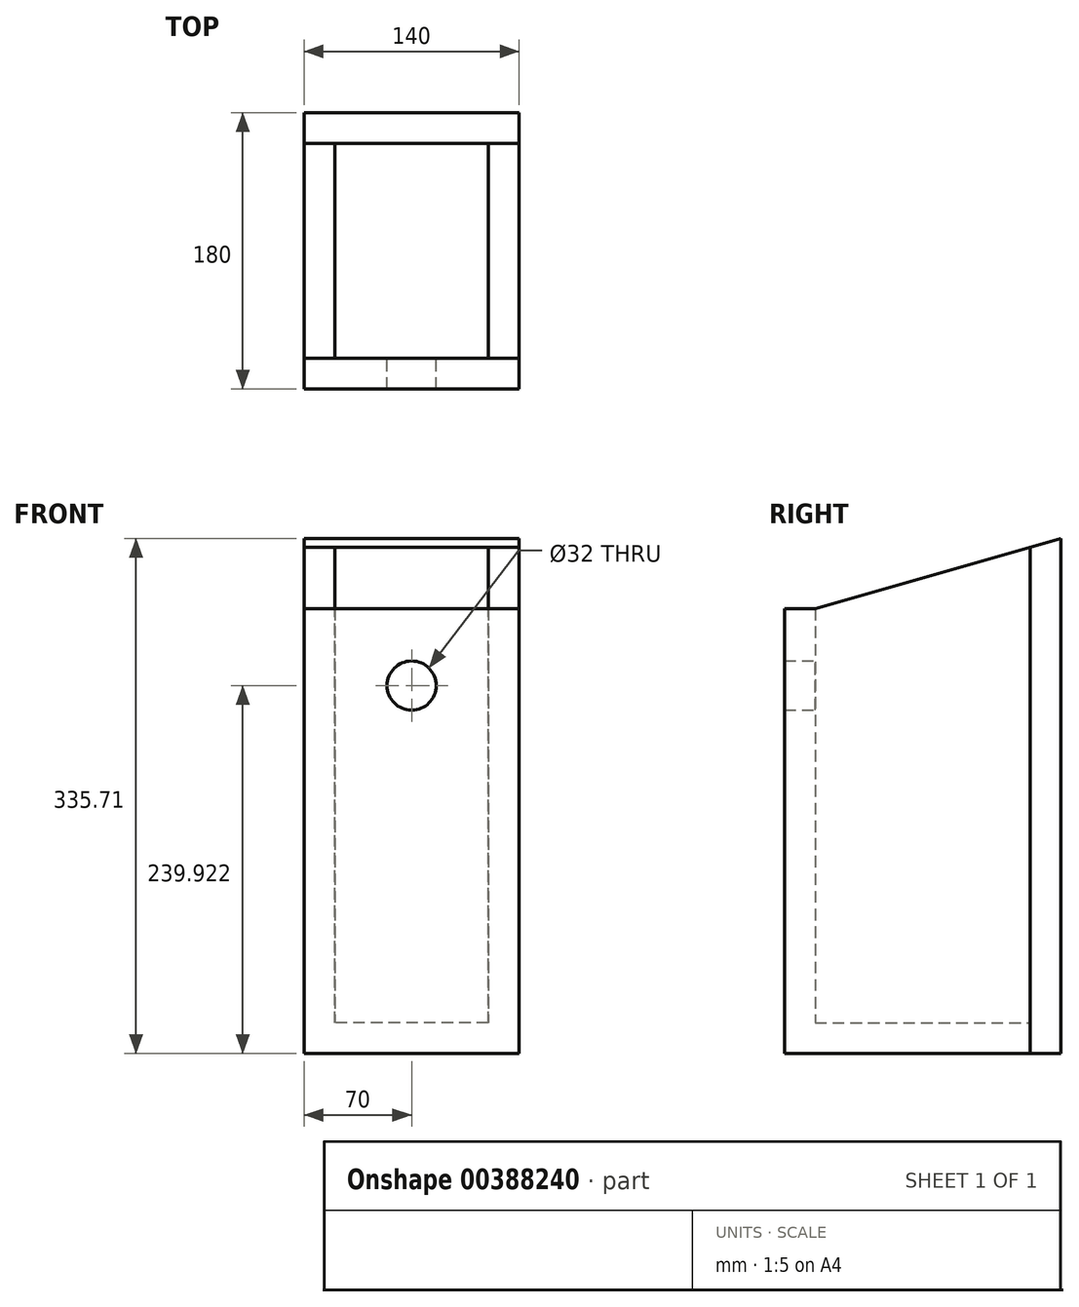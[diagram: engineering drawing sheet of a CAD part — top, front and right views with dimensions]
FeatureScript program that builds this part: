
annotation { "Feature Type Name" : "Feature", "Feature Type Description" : "" }
export const myFeature = defineFeature(function(context is Context, id is Id, definition is map)
    precondition{}
    {
        {
            var Q0;
            Q0=qCreatedBy(makeId("Top.planeOp"),FACE);
            var sketch = newSketch(context, id + "F0", { "sketchPlane" : qUnion([Q0])});
            skLineSegment(sketch, "E0.bottom", {"start": v(50, -70) * mm, "end": v(-50, -70) * mm});
            skLineSegment(sketch, "E0.top", {"start": v(50, 70) * mm, "end": v(-50, 70) * mm});
            skLineSegment(sketch, "E0.left", {"start": v(50, -70) * mm, "end": v(50, 70) * mm});
            skLineSegment(sketch, "E0.right", {"start": v(-50, -70) * mm, "end": v(-50, 70) * mm});
            skPoint(sketch, "E0.middle", {"position": v(0, 0) * mm});
            skSolve(sketch);
        }
        {
            var Q0;
            Q0 = qSketchRegion(id + "F0", true);
            extrude(context, id + "F1", {"entities" : qUnion([Q0]), "depth" : 20 * mm});
        }
        {
            var Q0;
            Q0=makeQuery(id+"F1.opExtrude","SWEPT_FACE",FACE,{"disambiguationData":[OSD([sQuery(id+"F0.wireOp",EDGE,"E0.bottom")])]});
            var sketch = newSketch(context, id + "F2", { "sketchPlane" : qUnion([Q0])});
            skLineSegment(sketch, "E1", {"start": v(-70, -0.08) * mm, "end": v(-70, 289.92) * mm});
            skLineSegment(sketch, "E2", {"start": v(-70, 289.92) * mm, "end": v(70, 289.92) * mm});
            skLineSegment(sketch, "E3", {"start": v(70, 289.92) * mm, "end": v(70, 0) * mm});
            skLineSegment(sketch, "E4", {"start": v(70, 0) * mm, "end": v(-70, 0) * mm});
            skCircle(sketch, "E5", {"center": v(0, 239.92) * mm, "radius": 16 * mm});
            skPoint(sketch, "E5.centerSnap0", {"position": v(0, 289.92) * mm});
            skSolve(sketch);
        }
        {
            var Q0;
            Q0 = qSketchRegion(id + "F2", true);
            extrude(context, id + "F3", {"entities" : qUnion([Q0]), "depth" : 20 * mm});
        }
        {
            var Q0;
            Q0=makeQuery(id+"F1.opExtrude","SWEPT_FACE",FACE,{"disambiguationData":[OSD([sQuery(id+"F0.wireOp",EDGE,"E0.right")])]});
            var sketch = newSketch(context, id + "F4", { "sketchPlane" : qUnion([Q0])});
            skLineSegment(sketch, "E6", {"start": v(-70, 0) * mm, "end": v(-70, 330) * mm});
            skLineSegment(sketch, "E7", {"start": v(-70, 330) * mm, "end": v(70, 290) * mm});
            skLineSegment(sketch, "E8", {"start": v(70, 290) * mm, "end": v(70, 0) * mm});
            skLineSegment(sketch, "E9", {"start": v(70, 0) * mm, "end": v(-70, 0) * mm});
            skSolve(sketch);
        }
        {
            var Q0;
            Q0 = qSketchRegion(id + "F4", true);
            extrude(context, id + "F5", {"entities" : qUnion([Q0]), "depth" : 20 * mm});
        }
        {
            var Q0;
            Q0=makeQuery(id+"F5.opExtrude","SWEPT_BODY",BODY,{"disambiguationData":[OSD([sQuery(id+"F4.wireOp",EDGE,"E6"),sQuery(id+"F4.wireOp",EDGE,"E7"),sQuery(id+"F4.wireOp",EDGE,"E8"),sQuery(id+"F4.wireOp",EDGE,"E9")])]});
            var Q1;
            Q1=qCreatedBy(makeId("Right.planeOp"),FACE);
            mirror(context, id + "F6", {"operationType" : NewBodyOperationType.ADD, "entities" : qUnion([Q0]), "mirrorPlane" : qUnion([Q1])});
        }
        {
            var Q0;
            Q0=makeQuery(id+"F5.opExtrude","CAP_FACE",FACE,{"disambiguationData":[OSD([sQuery(id+"F4.wireOp",EDGE,"E6"),sQuery(id+"F4.wireOp",EDGE,"E7"),sQuery(id+"F4.wireOp",EDGE,"E8"),sQuery(id+"F4.wireOp",EDGE,"E9")])],"isStart":false});
            var sketch = newSketch(context, id + "F7", { "sketchPlane" : qUnion([Q0])});
            skLineSegment(sketch, "E10", {"start": v(-70, 330) * mm, "end": v(-90, 335.71) * mm});
            skLineSegment(sketch, "E11", {"start": v(-90, 335.71) * mm, "end": v(-90, 0) * mm});
            skLineSegment(sketch, "E12", {"start": v(-90, 0) * mm, "end": v(-70, 0) * mm});
            skLineSegment(sketch, "E13", {"start": v(-70, 0) * mm, "end": v(-70, 330) * mm});
            skSolve(sketch);
        }
        {
            var Q0;
            Q0 = qSketchRegion(id + "F7", true);
            extrude(context, id + "F8", {"entities" : qUnion([Q0]), "oppositeDirection" : true, "depth" : 140 * mm});
        }
    });
